# Revit family: Shower-Valve_Trim-KOHLER-Aleo-K-22788IN_1
name_source: partatom
category: Plumbing Fixtures
units: mm (PartAtom-declared; Revit-internal decimal feet)

## family parameters
Cut with Voids When Loaded = No
Host = Face
OmniClass Number = 23.31.17.00
OmniClass Title = Showers
Part Type = Normal
Room Calculation Point = No
Round Connector Dimension = Use Diameter
Shared = No

## types (1)
- RGD-Polished Rose Gold
    ADA Compliant = No
    Assembly Code = D2010
    CW Connection = Yes
    Cold Water Inlet = Cold Water Inlet
    Date Modified = 12/27/2022
    Default Elevation = 42"
    Description = Recessed Shower Trim + At135 Valve In Rose Gold
    Drain Included = No
    Faucet Hole Spacing = 0"
    Finish = Kohler-Metal-RGD-Polished_Rose_Gold
    Flow Rate = 0 GPM
    HW Connection = Yes
    Handle Clearance = 3 13/16"
    Height = 6 9/16"
    Hot Water Inlet = Hot Water Inlet
    Length = 3 7/8"
    Manufacturer = Kohler Co.
    Master Format 2014 = 22 42 23
    Master Format 2014 Name = Residential Showers
    Material = Premium Metal Construction
    Model = K-22788IN-4-RGD
    Pressure = 0.00 psi
    Product Name = Aleo
    Product Page URL = https://www.kohler.co.in
    Spout Reach = 0"
    Tempered Water Outlet = Tempered Water Outlet
    Type = 1
    URL = https://www.kohler.co.in
    Vent Connection = No
    Waste Connection = No
    Waste Water Outlet = Waste Water Outlet
    WaterSense Certified = No
    Width = 4 7/16"

## geometry (parser evidence)
native form markers: Sweep x5
no freeform markers — native parametric forms only
